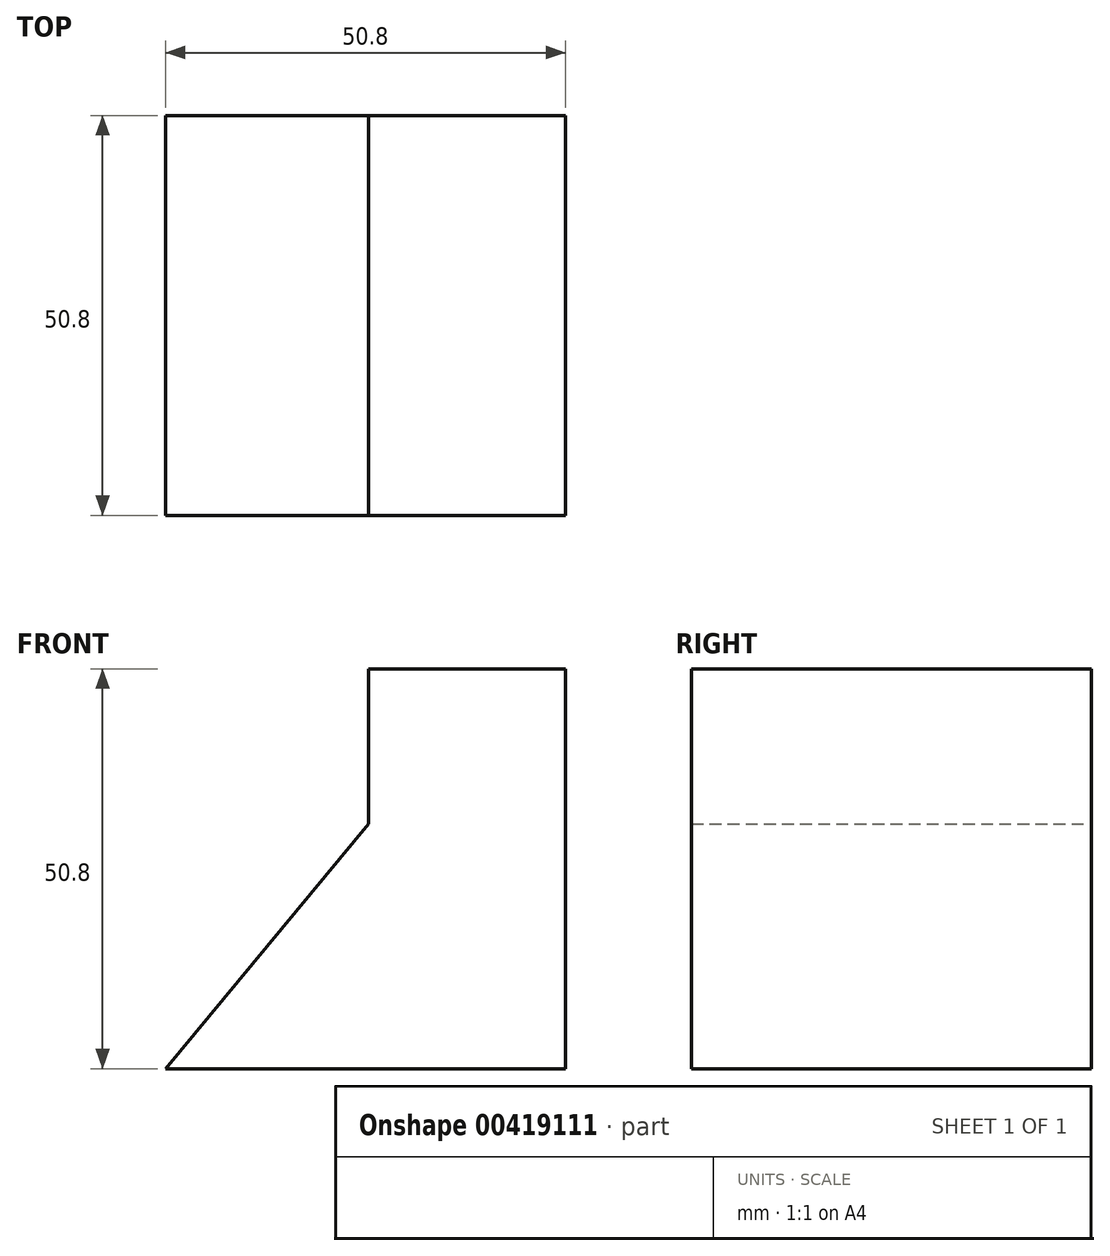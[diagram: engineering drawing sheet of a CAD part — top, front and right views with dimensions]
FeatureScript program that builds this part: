
annotation { "Feature Type Name" : "Feature", "Feature Type Description" : "" }
export const myFeature = defineFeature(function(context is Context, id is Id, definition is map)
    precondition{}
    {
        {
            var Q0;
            Q0=qCreatedBy(makeId("Front.planeOp"),FACE);
            var sketch = newSketch(context, id + "F0", { "sketchPlane" : qUnion([Q0])});
            skLineSegment(sketch, "E0", {"start": v(0, 0) * mm, "end": v(-50.8, 0) * mm});
            skLineSegment(sketch, "E1", {"start": v(0, 0) * mm, "end": v(0, 50.8) * mm});
            skLineSegment(sketch, "E2", {"start": v(0, 50.8) * mm, "end": v(-25.4, 50.8) * mm});
            skLineSegment(sketch, "E3", {"start": v(-25.01, 56.49) * mm, "end": v(-25.01, 31.09) * mm});
            skLineSegment(sketch, "E4", {"start": v(-25.01, 31.09) * mm, "end": v(-50.8, 0) * mm});
            skSolve(sketch);
        }
        {
            var Q0;
            Q0 = qSketchRegion(id + "F0", true);
            extrude(context, id + "F1", {"entities" : qUnion([Q0]), "depth" : 50.8 * mm});
        }
    });
